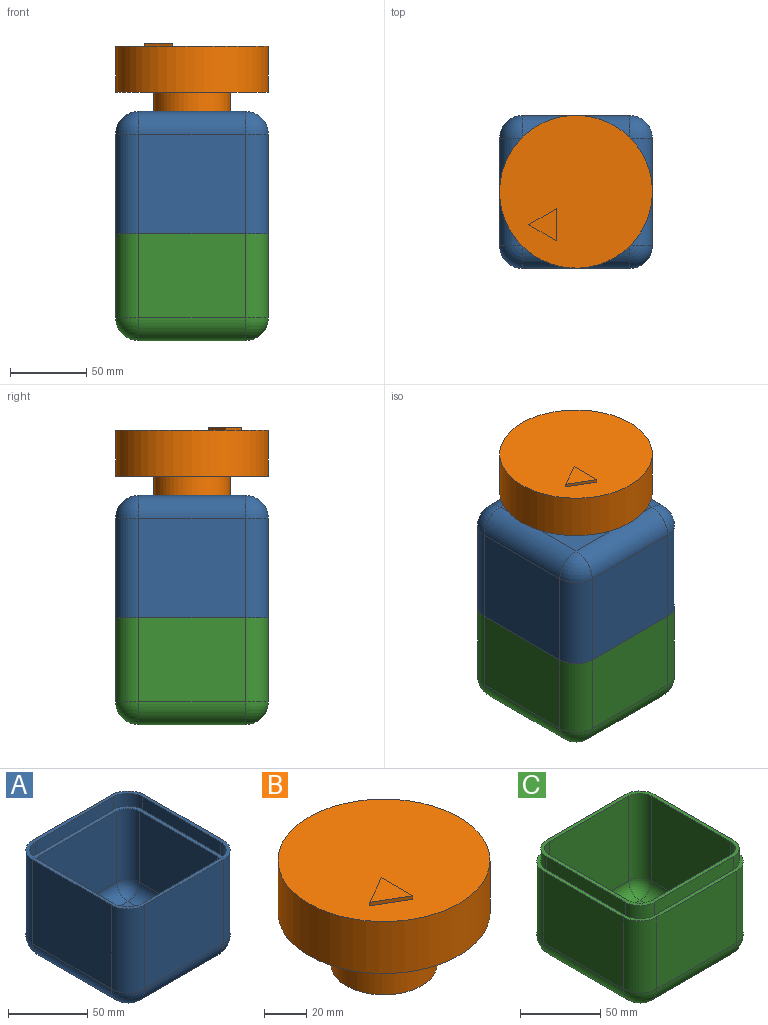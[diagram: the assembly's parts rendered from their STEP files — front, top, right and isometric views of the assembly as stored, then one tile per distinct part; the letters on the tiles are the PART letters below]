
ASSEMBLY  parts=3 mates=2
PART A: 45 faces, bbox 100x100x80 mm
  f0: plane 70x65mm, normal (1,0,0), area 4550mm2, adj f4,f11,f15,f17
  f1: plane 70x65mm, normal (0,1,0), area 4550mm2, adj f4,f8,f14,f17
  f2: plane 70x65mm, normal (-1,0,0), area 4550mm2, adj f4,f6,f8,f9
  f3: plane 70x65mm, normal (0,-1,0), area 4550mm2, adj f4,f6,f10,f11
  f4: plane 100x100mm, normal (0,0,1), area 916mm2, adj f0,f1,f2,f3,f6,f8,f11,f17
  f5: plane 70x70mm, normal (0,0,-1), area 2936.5mm2, adj f9,f10,f14,f15,f44
  f6: cylinder r=15mm len=65mm, axis (0,0,-1), area 1531.5mm2, adj f2,f3,f4,f7
  f7: sphere r=15mm, area 353.4mm2, adj f6,f9,f10
  f8: cylinder r=15mm len=65mm, axis (0,0,1), area 1531.5mm2, adj f1,f2,f4,f12
  f9: cylinder r=15mm len=70mm, axis (0,-1,0), area 1649.3mm2, adj f2,f5,f7,f12
  f10: cylinder r=15mm len=70mm, axis (1,0,0), area 1649.3mm2, adj f3,f5,f7,f13
  f11: cylinder r=15mm len=65mm, axis (0,0,1), area 1531.5mm2, adj f0,f3,f4,f13
  f12: sphere r=15mm, area 353.4mm2, adj f8,f9,f14
  f13: sphere r=15mm, area 353.4mm2, adj f10,f11,f15
  f14: cylinder r=15mm len=70mm, axis (-1,0,0), area 1649.3mm2, adj f1,f5,f12,f16
  f15: cylinder r=15mm len=70mm, axis (0,1,0), area 1649.3mm2, adj f0,f5,f13,f16
  f16: sphere r=15mm, area 353.4mm2, adj f14,f15,f17
  f17: cylinder r=15mm len=65mm, axis (0,0,-1), area 1531.5mm2, adj f0,f1,f4,f16
  f18: plane 95x95mm, normal (0,0,1), area 876.7mm2, adj f19,f20,f21,f22,f23,f24,f25,f26
  f19: cylinder r=12.5mm len=12.5mm, axis (0,0,1), area 196.3mm2, adj f4,f18,f20,f26
  f20: plane 70x10mm, normal (0,-1,0), area 700mm2, adj f4,f18,f19,f21
  f21: cylinder r=12.5mm len=12.5mm, axis (0,0,1), area 196.3mm2, adj f4,f18,f20,f22
  f22: plane 70x10mm, normal (1,0,0), area 700mm2, adj f4,f18,f21,f23
  f23: cylinder r=12.5mm len=12.5mm, axis (0,0,1), area 196.3mm2, adj f4,f18,f22,f24
  f24: plane 70x10mm, normal (0,1,0), area 700mm2, adj f4,f18,f23,f25
  f25: cylinder r=12.5mm len=12.5mm, axis (0,0,1), area 196.3mm2, adj f4,f18,f24,f26
  f26: plane 70x10mm, normal (-1,0,0), area 700mm2, adj f4,f18,f19,f25
  f27: plane 70x70mm, normal (0,0,1), area 2936.5mm2, adj f28,f29,f30,f31,f44
  f28: cylinder r=10mm len=70mm, axis (0,1,0), area 1099.6mm2, adj f27,f34,f35,f43
  f29: cylinder r=10mm len=70mm, axis (-1,0,0), area 1099.6mm2, adj f27,f33,f35,f42
  f30: cylinder r=10mm len=70mm, axis (0,-1,0), area 1099.6mm2, adj f27,f32,f33,f40
  f31: cylinder r=10mm len=70mm, axis (1,0,0), area 1099.6mm2, adj f27,f32,f34,f39
  f32: sphere r=10mm, area 157.1mm2, adj f30,f31,f37
  f33: sphere r=10mm, area 157.1mm2, adj f29,f30,f36
  f34: sphere r=10mm, area 157.1mm2, adj f28,f31,f38
  f35: sphere r=10mm, area 157.1mm2, adj f28,f29,f41
  f36: cylinder r=10mm len=55mm, axis (0,0,1), area 863.9mm2, adj f18,f33,f40,f42
  f37: cylinder r=10mm len=55mm, axis (0,0,-1), area 863.9mm2, adj f18,f32,f39,f40
  f38: cylinder r=10mm len=55mm, axis (0,0,1), area 863.9mm2, adj f18,f34,f39,f43
  f39: plane 70x55mm, normal (0,1,0), area 3850mm2, adj f18,f31,f37,f38
  f40: plane 70x55mm, normal (1,0,0), area 3850mm2, adj f18,f30,f36,f37
  f41: cylinder r=10mm len=55mm, axis (0,0,-1), area 863.9mm2, adj f18,f35,f42,f43
  f42: plane 70x55mm, normal (0,-1,0), area 3850mm2, adj f18,f29,f36,f41
  f43: plane 70x55mm, normal (-1,0,0), area 3850mm2, adj f18,f28,f38,f41
  f44: cylinder r=25mm len=50mm, axis (0,0,-1), area 785.4mm2, adj f5,f27
PART B: 9 faces, bbox 100x100x62 mm
  f0: plane 50x50mm, normal (0,0,-1), area 1963.5mm2, adj f1
  f1: cylinder r=25mm len=50mm, axis (0,0,-1), area 4712.4mm2, adj f0,f2
  f2: plane 100x100mm, normal (0,0,-1), area 5890.5mm2, adj f1,f3
  f3: cylinder r=50mm len=100mm, axis (0,0,-1), area 9424.8mm2, adj f2,f4
  f4: plane 100x100mm, normal (0,0,1), area 7662.6mm2, adj f3,f5,f6,f7
  f5: plane 18.21x10.51mm, normal (-0.5,0.87,0), area 42mm2, adj f4,f6,f7,f8
  f6: plane 18.21x10.51mm, normal (-0.5,-0.87,0), area 42mm2, adj f4,f5,f7,f8
  f7: plane 21.02x2mm, normal (1,0,0), area 42mm2, adj f4,f5,f6,f8
  f8: plane 21.02x18.21mm, normal (0,0,1), area 191.4mm2, adj f5,f6,f7
PART C: 44 faces, bbox 100x100x80 mm
  f0: plane 95x95mm, normal (0,0,1), area 876.7mm2, adj f1,f2,f3,f4,f6,f8,f11,f17
  f1: plane 70x65mm, normal (0,1,0), area 4550mm2, adj f0,f11,f15,f17
  f2: plane 70x65mm, normal (-1,0,0), area 4550mm2, adj f0,f8,f14,f17
  f3: plane 70x65mm, normal (0,-1,0), area 4550mm2, adj f0,f6,f8,f9
  f4: plane 70x65mm, normal (1,0,0), area 4550mm2, adj f0,f6,f10,f11
  f5: plane 70x70mm, normal (0,0,1), area 4900mm2, adj f9,f10,f14,f15
  f6: cylinder r=10mm len=65mm, axis (0,0,1), area 1021mm2, adj f0,f3,f4,f7
  f7: sphere r=10mm, area 157.1mm2, adj f6,f9,f10
  f8: cylinder r=10mm len=65mm, axis (0,0,-1), area 1021mm2, adj f0,f2,f3,f12
  f9: cylinder r=10mm len=70mm, axis (-1,0,0), area 1099.6mm2, adj f3,f5,f7,f12
  f10: cylinder r=10mm len=70mm, axis (0,-1,0), area 1099.6mm2, adj f4,f5,f7,f13
  f11: cylinder r=10mm len=65mm, axis (0,0,-1), area 1021mm2, adj f0,f1,f4,f13
  f12: sphere r=10mm, area 157.1mm2, adj f8,f9,f14
  f13: sphere r=10mm, area 157.1mm2, adj f10,f11,f15
  f14: cylinder r=10mm len=70mm, axis (0,1,0), area 1099.6mm2, adj f2,f5,f12,f16
  f15: cylinder r=10mm len=70mm, axis (1,0,0), area 1099.6mm2, adj f1,f5,f13,f16
  f16: sphere r=10mm, area 157.1mm2, adj f14,f15,f17
  f17: cylinder r=10mm len=65mm, axis (0,0,1), area 1021mm2, adj f0,f1,f2,f16
  f18: cylinder r=12.5mm len=12.5mm, axis (0,0,1), area 196.3mm2, adj f0,f19,f25,f26
  f19: plane 70x10mm, normal (0,-1,0), area 700mm2, adj f0,f18,f20,f26
  f20: cylinder r=12.5mm len=12.5mm, axis (0,0,1), area 196.3mm2, adj f0,f19,f21,f26
  f21: plane 70x10mm, normal (-1,0,0), area 700mm2, adj f0,f20,f22,f26
  f22: cylinder r=12.5mm len=12.5mm, axis (0,0,1), area 196.3mm2, adj f0,f21,f23,f26
  f23: plane 70x10mm, normal (0,1,0), area 700mm2, adj f0,f22,f24,f26
  f24: cylinder r=12.5mm len=12.5mm, axis (0,0,1), area 196.3mm2, adj f0,f23,f25,f26
  f25: plane 70x10mm, normal (1,0,0), area 700mm2, adj f0,f18,f24,f26
  f26: plane 100x100mm, normal (0,0,1), area 916mm2, adj f18,f19,f20,f21,f22,f23,f24,f25
  f27: plane 70x70mm, normal (0,0,-1), area 4900mm2, adj f28,f29,f30,f31
  f28: cylinder r=15mm len=70mm, axis (1,0,0), area 1649.3mm2, adj f27,f34,f35,f43
  f29: cylinder r=15mm len=70mm, axis (0,1,0), area 1649.3mm2, adj f27,f33,f35,f42
  f30: cylinder r=15mm len=70mm, axis (-1,0,0), area 1649.3mm2, adj f27,f32,f33,f40
  f31: cylinder r=15mm len=70mm, axis (0,-1,0), area 1649.3mm2, adj f27,f32,f34,f38
  f32: sphere r=15mm, area 353.4mm2, adj f30,f31,f36
  f33: sphere r=15mm, area 353.4mm2, adj f29,f30,f39
  f34: sphere r=15mm, area 353.4mm2, adj f28,f31,f37
  f35: sphere r=15mm, area 353.4mm2, adj f28,f29,f41
  f36: cylinder r=15mm len=55mm, axis (0,0,1), area 1295.9mm2, adj f26,f32,f38,f40
  f37: cylinder r=15mm len=55mm, axis (0,0,-1), area 1295.9mm2, adj f26,f34,f38,f43
  f38: plane 70x55mm, normal (-1,0,0), area 3850mm2, adj f26,f31,f36,f37
  f39: cylinder r=15mm len=55mm, axis (0,0,-1), area 1295.9mm2, adj f26,f33,f40,f42
  f40: plane 70x55mm, normal (0,1,0), area 3850mm2, adj f26,f30,f36,f39
  f41: cylinder r=15mm len=55mm, axis (0,0,1), area 1295.9mm2, adj f26,f35,f42,f43
  f42: plane 70x55mm, normal (1,0,0), area 3850mm2, adj f26,f29,f39,f41
  f43: plane 70x55mm, normal (0,-1,0), area 3850mm2, adj f26,f28,f37,f41
PLACE A rot(axis=(0,1,0),180deg) t=(0,0,150)mm
PLACE B t=(0,0,132.5)mm
PLACE C at identity fixed
MATE fastened C.f19 <-> A.f24  axis (0,-1,0) through (0,-47.5,75)mm
MATE revolute B.f1 <-> A.f44  axis (0,0,-1) through (0,0,147.5)mm
